# Revit family: Lockin Lockers AU_Mini Locker_R22
name_source: partatom
category: Furniture
units: mm (PartAtom-declared; Revit-internal decimal feet)

## family parameters
Always vertical = Yes
Cut with Voids When Loaded = No
OmniClass Number = 23.40.20.27
OmniClass Title = Storage Shelving
Render Appearance Source = Family Geometry
Room Calculation Point = No
Shared = Yes
Work Plane-Based = Yes

## types (7) — shared parameters
Body/Frame Material = Material - Melamine - Laminex or Polytec Finish
Depth Control = 200 mm  [stored 0.656168 ft]
Desired Depth = 200 mm  [stored 0.656168 ft]
Desired Width = 250 mm  [stored 0.82021 ft]
Door Material = Material - Melamine - Laminex or Polytec Finish
Door Type = Lockin_Locker Door_Standard_R22 : Standard Door/Combination Lock
Locker Joint = 3 mm  [stored 0.00984252 ft]
Manufacturer = Lockin Lockers AU
Maximum Depth = 400 mm  [stored 1.31234 ft]
Maximum Width = 220 mm  [stored 0.721785 ft]
Minimum Depth = 200 mm  [stored 0.656168 ft]
Minimum Width = 160 mm  [stored 0.524934 ft]
TH Wall = 18 mm  [stored 0.0590551 ft]
URL = https://www.lockin.com.au
Width Control = 220 mm  [stored 0.721785 ft]
zero-valued in all types: Default Elevation

## per-type parameters (varying)
| type | Description | Desired Height | H Locker | Height Control | Maximum Height | Minimum Height | Model | N_Doors | N_Shelves |
| Mini Locker 2 door (ML2) | Mini Locker 2 door | 360 mm  [stored 1.1811 ft] | 178.5 mm  [stored 0.58563 ft] | 360 mm  [stored 1.1811 ft] | 400 mm  [stored 1.31234 ft] | 320 mm  [stored 1.04987 ft] | ML2 | 2 | 2 |
| Mini Locker 8 door (ML8) | Mini Locker 8 door | 1440 mm  [stored 4.72441 ft] | 177.38 mm | 1440 mm  [stored 4.72441 ft] | 1600 mm  [stored 5.24934 ft] | 1280 mm  [stored 4.19948 ft] | ML8 | 8 | 8 |
| Mini Locker 3 door (ML3) | Mini Locker 3 door | 540 mm  [stored 1.77165 ft] | 178 mm  [stored 0.58399 ft] | 540 mm  [stored 1.77165 ft] | 600 mm | 480 mm  [stored 1.5748 ft] | ML3 | 3 | 3 |
| Mini Locker 4 door (ML4) | Mini Locker 4 door | 720 mm  [stored 2.3622 ft] | 177.75 mm  [stored 0.583169 ft] | 720 mm  [stored 2.3622 ft] | 800 mm  [stored 2.62467 ft] | 640 mm  [stored 2.09974 ft] | ML4 | 4 | 4 |
| Mini Locker 5 door (ML5) | Mini Locker 5 door | 900 mm  [stored 2.95276 ft] | 177.6 mm  [stored 0.582677 ft] | 900 mm  [stored 2.95276 ft] | 1000 mm  [stored 3.28084 ft] | 800 mm  [stored 2.62467 ft] | ML5 | 5 | 5 |
| Mini Locker 6 door (ML6) | Mini Locker 6 door | 1080 mm  [stored 3.54331 ft] | 177.5 mm | 1080 mm  [stored 3.54331 ft] | 1200 mm | 960 mm  [stored 3.14961 ft] | ML6 | 6 | 6 |
| Mini Locker 7 door (ML7) | Mini Locker 7 door | 1260 mm  [stored 4.13386 ft] | 177.43 mm | 1260 mm  [stored 4.13386 ft] | 1400 mm  [stored 4.59318 ft] | 1120 mm  [stored 3.67454 ft] | ML7 | 7 | 7 |

note: [stored X ft] marks values corroborated as IEEE doubles in the binary element streams (Revit-internal decimal feet)

## geometry (parser evidence)
native form markers: Sweep x3
no freeform markers — native parametric forms only
